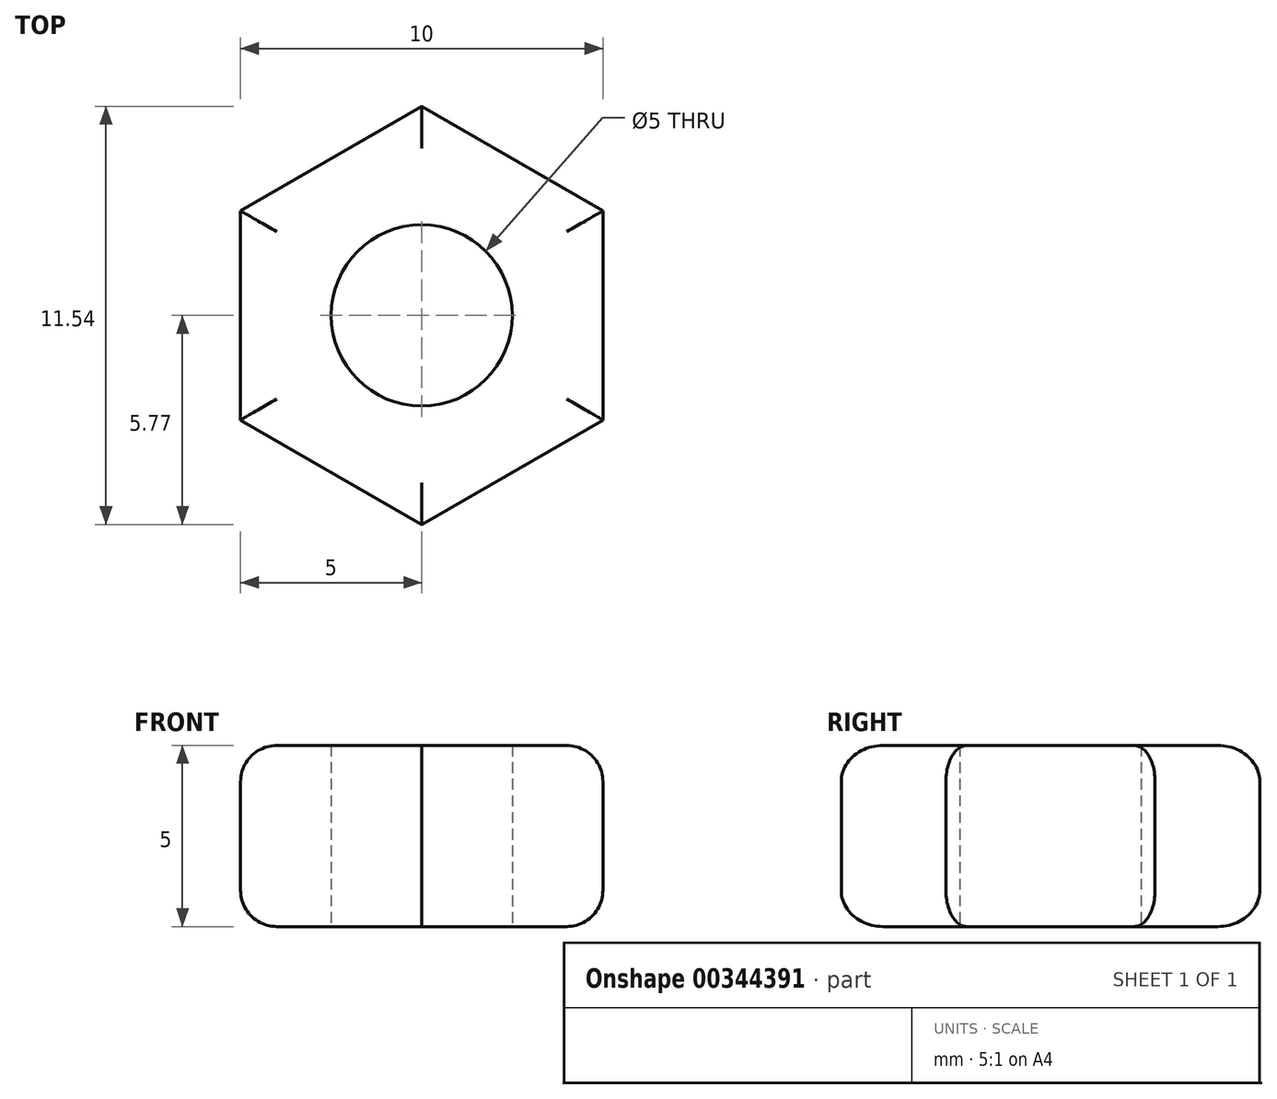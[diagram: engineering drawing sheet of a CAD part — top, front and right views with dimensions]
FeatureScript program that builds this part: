
annotation { "Feature Type Name" : "Feature", "Feature Type Description" : "" }
export const myFeature = defineFeature(function(context is Context, id is Id, definition is map)
    precondition{}
    {
        {
            var Q0;
            Q0=qCreatedBy(makeId("Top.planeOp"),FACE);
            var sketch = newSketch(context, id + "F0", { "sketchPlane" : qUnion([Q0])});
            skCircle(sketch, "E0.cCircle", {"center": v(0, 0) * mm, "radius": 5 * mm, "construction": true});
            skLineSegment(sketch, "E0.0", {"start": v(5, -2.89) * mm, "end": v(0, -5.77) * mm});
            skLineSegment(sketch, "E0.1", {"start": v(0, -5.77) * mm, "end": v(-5, -2.89) * mm});
            skLineSegment(sketch, "E0.2", {"start": v(-5, -2.89) * mm, "end": v(-5, 2.89) * mm});
            skLineSegment(sketch, "E0.3", {"start": v(-5, 2.89) * mm, "end": v(0, 5.77) * mm});
            skLineSegment(sketch, "E0.4", {"start": v(0, 5.77) * mm, "end": v(5, 2.89) * mm});
            skLineSegment(sketch, "E0.5", {"start": v(5, 2.89) * mm, "end": v(5, -2.89) * mm});
            skPoint(sketch, "E0.0.midPoint", {"position": v(2.5, -4.33) * mm});
            skCircle(sketch, "E1", {"center": v(0, 0) * mm, "radius": 2.5 * mm});
            skSolve(sketch);
        }
        {
            var Q0;
            Q0=makeQuery(id+"F0.imprint","IMPRINT",FACE,{"disambiguationData":[TD([[makeQuery(id+"F0.imprint","IMPRINT",EDGE,{"derivedFrom":sQuery(id+"F0.wireOp",EDGE,"E0.0")}),-1.0]])]});
            extrude(context, id + "F1", {"entities" : qUnion([Q0]), "depth" : 5 * mm});
        }
        {
            var Q0;
            Q0=makeQuery(id+"F1.opExtrude","CAP_EDGE",EDGE,{"disambiguationData":[OSD([sQuery(id+"F0.wireOp",EDGE,"E0.5")])],"isStart":false});
            var Q1;
            Q1=makeQuery(id+"F1.opExtrude","CAP_EDGE",EDGE,{"disambiguationData":[OSD([sQuery(id+"F0.wireOp",EDGE,"E0.0")])],"isStart":false});
            var Q2;
            Q2=makeQuery(id+"F1.opExtrude","CAP_EDGE",EDGE,{"disambiguationData":[OSD([sQuery(id+"F0.wireOp",EDGE,"E0.1")])],"isStart":false});
            var Q3;
            Q3=makeQuery(id+"F1.opExtrude","CAP_EDGE",EDGE,{"disambiguationData":[OSD([sQuery(id+"F0.wireOp",EDGE,"E0.2")])],"isStart":false});
            var Q4;
            Q4=makeQuery(id+"F1.opExtrude","CAP_EDGE",EDGE,{"disambiguationData":[OSD([sQuery(id+"F0.wireOp",EDGE,"E0.3")])],"isStart":false});
            var Q5;
            Q5=makeQuery(id+"F1.opExtrude","CAP_EDGE",EDGE,{"disambiguationData":[OSD([sQuery(id+"F0.wireOp",EDGE,"E0.4")])],"isStart":false});
            var Q6;
            Q6=makeQuery(id+"F1.opExtrude","CAP_EDGE",EDGE,{"disambiguationData":[OSD([sQuery(id+"F0.wireOp",EDGE,"E0.5")])],"isStart":true});
            var Q7;
            Q7=makeQuery(id+"F1.opExtrude","CAP_EDGE",EDGE,{"disambiguationData":[OSD([sQuery(id+"F0.wireOp",EDGE,"E0.0")])],"isStart":true});
            var Q8;
            Q8=makeQuery(id+"F1.opExtrude","CAP_EDGE",EDGE,{"disambiguationData":[OSD([sQuery(id+"F0.wireOp",EDGE,"E0.1")])],"isStart":true});
            var Q9;
            Q9=makeQuery(id+"F1.opExtrude","CAP_EDGE",EDGE,{"disambiguationData":[OSD([sQuery(id+"F0.wireOp",EDGE,"E0.4")])],"isStart":true});
            var Q10;
            Q10=makeQuery(id+"F1.opExtrude","CAP_EDGE",EDGE,{"disambiguationData":[OSD([sQuery(id+"F0.wireOp",EDGE,"E0.3")])],"isStart":true});
            var Q11;
            Q11=makeQuery(id+"F1.opExtrude","CAP_EDGE",EDGE,{"disambiguationData":[OSD([sQuery(id+"F0.wireOp",EDGE,"E0.2")])],"isStart":true});
            fillet(context, id + "F2", {"entities" : qUnion([Q0, Q1, Q2, Q3, Q4, Q5, Q6, Q7, Q8, Q9, Q10, Q11]), "radius" : 1 * mm, "tangentPropagation" : true, "allowEdgeOverflow" : false});
        }
    });
